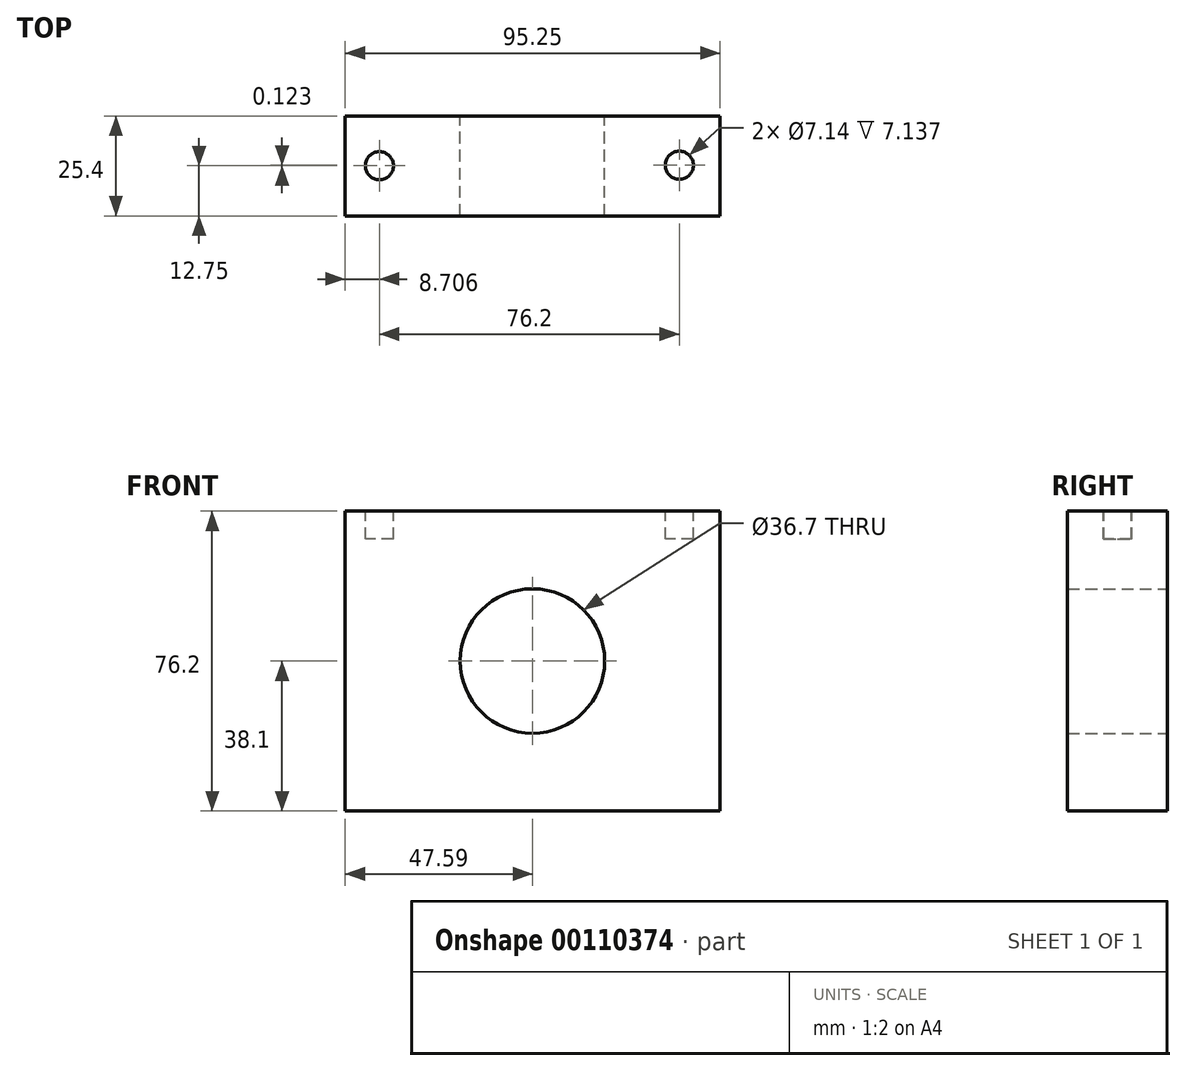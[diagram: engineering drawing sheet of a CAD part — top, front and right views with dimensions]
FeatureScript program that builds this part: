
annotation { "Feature Type Name" : "Feature", "Feature Type Description" : "" }
export const myFeature = defineFeature(function(context is Context, id is Id, definition is map)
    precondition{}
    {
        {
            var Q0;
            Q0=qCreatedBy(makeId("Front.planeOp"),FACE);
            var sketch = newSketch(context, id + "F0", { "sketchPlane" : qUnion([Q0])});
            skLineSegment(sketch, "E0", {"start": v(-47.6, 38.1) * mm, "end": v(-47.6, -38.1) * mm});
            skLineSegment(sketch, "E1", {"start": v(47.66, 38.1) * mm, "end": v(47.66, -38.1) * mm});
            skLineSegment(sketch, "E2", {"start": v(47.66, -38.1) * mm, "end": v(-47.6, -38.1) * mm});
            skLineSegment(sketch, "E3", {"start": v(-47.6, 38.1) * mm, "end": v(47.66, 38.1) * mm});
            skCircle(sketch, "E4", {"center": v(0, 0) * mm, "radius": 18.35 * mm});
            skLineSegment(sketch, "E5", {"start": v(18.35, 0) * mm, "end": v(47.66, 0) * mm});
            skPoint(sketch, "E5.endSnap0", {"position": v(47.66, 0) * mm});
            skLineSegment(sketch, "E6", {"start": v(-18.35, 0) * mm, "end": v(-47.6, 0) * mm});
            skPoint(sketch, "E7.start.orphan", {"position": v(0, -18.35) * mm});
            skSolve(sketch);
        }
        {
            var Q0;
            {var subQ3=sQuery(id+"F0.wireOp",EDGE,"E3");Q0=makeQuery(id+"F0.imprint","IMPRINT",FACE,{"disambiguationData":[TD([[makeQuery(id+"F0.imprint","IMPRINT",EDGE,{"derivedFrom":subQ3}),-1.0]])]});}
            var Q1;
            {var subQ3=sQuery(id+"F0.wireOp",EDGE,"E2");Q1=makeQuery(id+"F0.imprint","IMPRINT",FACE,{"disambiguationData":[TD([[makeQuery(id+"F0.imprint","IMPRINT",EDGE,{"derivedFrom":subQ3}),-1.0]])]});}
            var Q2;
            Q2 = qSketchRegion(id + "F2", true);
            extrude(context, id + "F1", {"entities" : qUnion([Q0, Q1, Q2]), "depth" : 25.4 * mm});
        }
        {
            var Q0;
            Q0=makeQuery(id+"F1.opExtrude","SWEPT_FACE",FACE,{"disambiguationData":[OSD([sQuery(id+"F0.wireOp",EDGE,"E3")])]});
            var sketch = newSketch(context, id + "F2", { "sketchPlane" : qUnion([Q0])});
            skCircle(sketch, "E8", {"center": v(-38.88, -12.65) * mm, "radius": 3.57 * mm});
            skCircle(sketch, "E9", {"center": v(37.32, -12.53) * mm, "radius": 3.57 * mm});
            skSolve(sketch);
        }
        {
            var Q0;
            Q0=makeQuery(id+"F2.imprint","IMPRINT",FACE,{"disambiguationData":[TD([[makeQuery(id+"F2.imprint","IMPRINT",EDGE,{"derivedFrom":sQuery(id+"F2.wireOp",EDGE,"E9")}),1.0]])]});
            var Q1;
            Q1=makeQuery(id+"F1.opExtrude","SWEPT_FACE",FACE,{"disambiguationData":[OSD([sQuery(id+"F0.wireOp",EDGE,"E3")])]});
            extrude(context, id + "F3", {"entities" : qUnion([Q0]), "operationType" : NewBodyOperationType.REMOVE, "oppositeDirection" : true, "endBoundEntityFace" : qUnion([Q1]), "depth" : 7.14 * mm});
        }
        {
            var Q0;
            Q0 = qSketchRegion(id + "F2", true);
            extrude(context, id + "F4", {"entities" : qUnion([Q0]), "operationType" : NewBodyOperationType.REMOVE, "oppositeDirection" : true, "depth" : 7.14 * mm});
        }
    });
